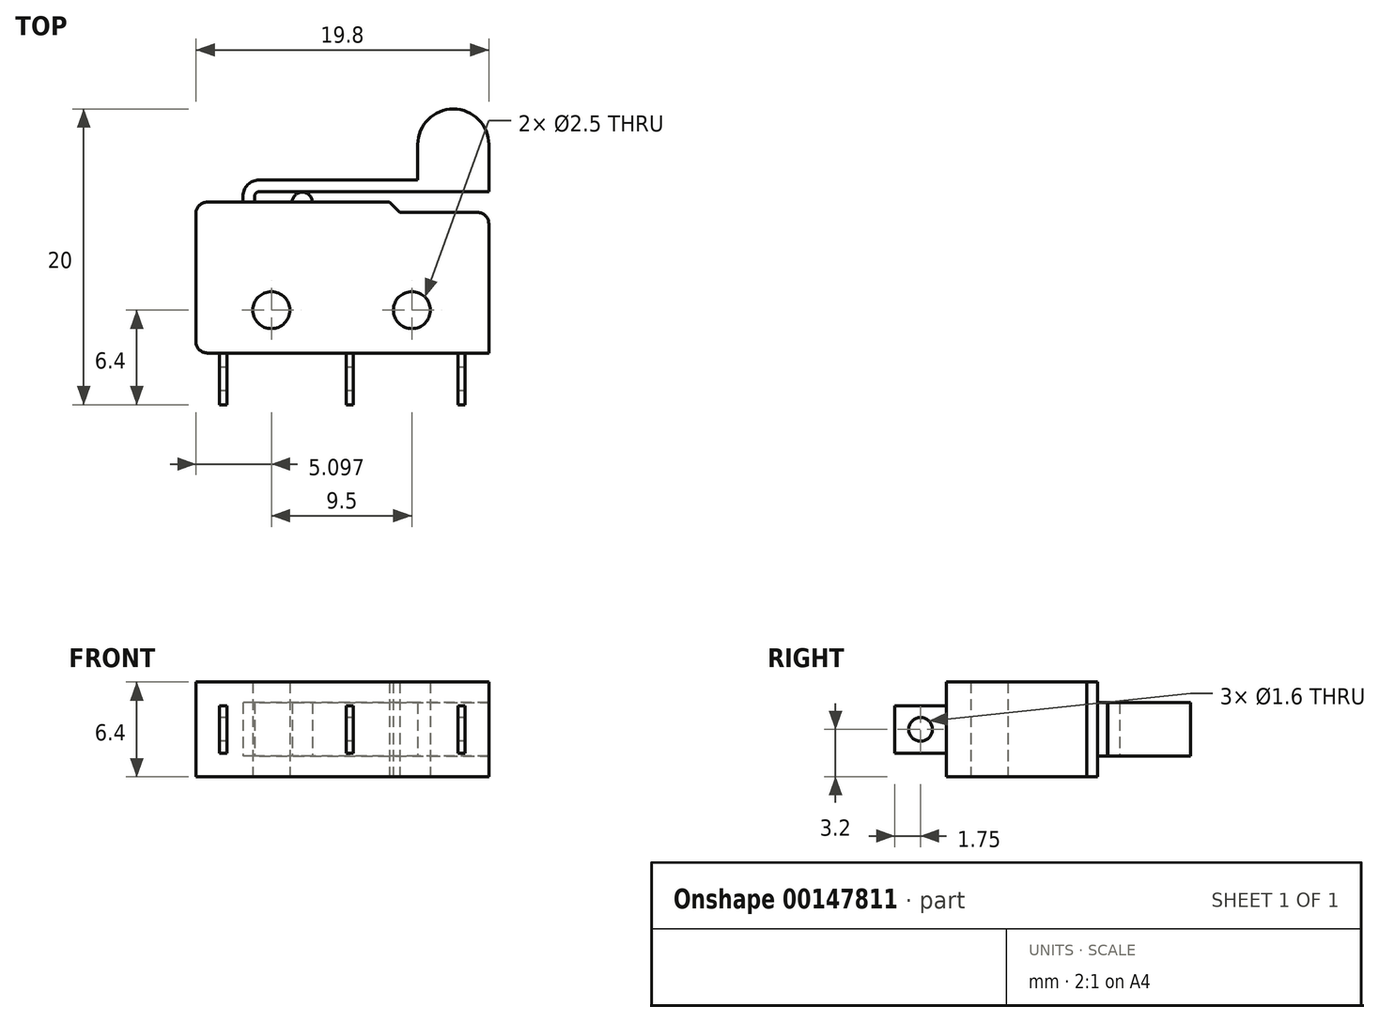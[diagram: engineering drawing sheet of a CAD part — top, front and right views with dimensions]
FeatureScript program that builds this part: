
annotation { "Feature Type Name" : "Feature", "Feature Type Description" : "" }
export const myFeature = defineFeature(function(context is Context, id is Id, definition is map)
    precondition{}
    {
        {
            var Q0;
            Q0=qCreatedBy(makeId("Top.planeOp"),FACE);
            var sketch = newSketch(context, id + "F0", { "sketchPlane" : qUnion([Q0])});
            skLineSegment(sketch, "E0", {"start": v(0, 0) * mm, "end": v(6.02, 0) * mm});
            skLineSegment(sketch, "E1", {"start": v(6.02, 0) * mm, "end": v(6.02, -9.5) * mm});
            skLineSegment(sketch, "E2", {"start": v(0, 0) * mm, "end": v(-0.7, 0.7) * mm});
            skLineSegment(sketch, "E3", {"start": v(6.02, 0) * mm, "end": v(6.02, 0.7) * mm, "construction": true});
            skLineSegment(sketch, "E4", {"start": v(-0.7, 0.7) * mm, "end": v(6.02, 0.7) * mm, "construction": true});
            skLineSegment(sketch, "E5.bottom", {"start": v(4.42, -9.5) * mm, "end": v(3.92, -9.5) * mm});
            skLineSegment(sketch, "E5.top", {"start": v(4.42, -13) * mm, "end": v(3.92, -13) * mm});
            skLineSegment(sketch, "E5.left", {"start": v(3.92, -9.5) * mm, "end": v(3.92, -13) * mm});
            skLineSegment(sketch, "E5.right", {"start": v(4.42, -9.5) * mm, "end": v(4.42, -13) * mm});
            skLineSegment(sketch, "E6.bottom", {"start": v(-3.13, -9.5) * mm, "end": v(-3.63, -9.5) * mm});
            skLineSegment(sketch, "E6.top", {"start": v(-3.13, -13) * mm, "end": v(-3.63, -13) * mm});
            skLineSegment(sketch, "E6.left", {"start": v(-3.13, -9.5) * mm, "end": v(-3.13, -13) * mm});
            skLineSegment(sketch, "E6.right", {"start": v(-3.63, -9.5) * mm, "end": v(-3.63, -13) * mm});
            skLineSegment(sketch, "E7.top", {"start": v(-11.68, -13) * mm, "end": v(-12.18, -13) * mm});
            skLineSegment(sketch, "E7.left", {"start": v(-12.18, -9.5) * mm, "end": v(-12.18, -13) * mm});
            skLineSegment(sketch, "E7.right", {"start": v(-11.68, -9.5) * mm, "end": v(-11.68, -13) * mm});
            skLineSegment(sketch, "E8", {"start": v(-0.7, 0.7) * mm, "end": v(-5.91, 0.7) * mm});
            skLineSegment(sketch, "E9", {"start": v(-5.91, 0.7) * mm, "end": v(-7.27, 0.7) * mm, "construction": true});
            skArc(sketch, "E10", {"start": v(-5.91, 0.7) * mm, "mid": v(-6.6, 1.38) * mm, "end": v(-7.27, 0.7) * mm});
            skLineSegment(sketch, "E11", {"start": v(-7.27, 0.7) * mm, "end": v(-9.81, 0.7) * mm});
            skLineSegment(sketch, "E12", {"start": v(-9.81, 0.7) * mm, "end": v(-9.81, 1.1) * mm});
            skArc(sketch, "E13", {"start": v(-9.51, 1.4) * mm, "mid": v(-9.73, 1.32) * mm, "end": v(-9.81, 1.1) * mm});
            skLineSegment(sketch, "E14", {"start": v(-9.51, 1.4) * mm, "end": v(6.02, 1.4) * mm});
            skLineSegment(sketch, "E15", {"start": v(6.02, 1.4) * mm, "end": v(6.02, 2.2) * mm});
            skLineSegment(sketch, "E16", {"start": v(1.22, 2.2) * mm, "end": v(-9.51, 2.2) * mm});
            skArc(sketch, "E17", {"start": v(-9.51, 2.2) * mm, "mid": v(-10.29, 1.88) * mm, "end": v(-10.6, 1.1) * mm});
            skLineSegment(sketch, "E18", {"start": v(-10.6, 1.1) * mm, "end": v(-10.6, 0.7) * mm});
            skLineSegment(sketch, "E19", {"start": v(-10.6, 0.7) * mm, "end": v(-9.81, 0.7) * mm});
            skLineSegment(sketch, "E20", {"start": v(-8.68, -9.5) * mm, "end": v(-8.68, -6.6) * mm, "construction": true});
            skLineSegment(sketch, "E21", {"start": v(-8.68, -6.6) * mm, "end": v(-13.78, -6.6) * mm, "construction": true});
            skLineSegment(sketch, "E22", {"start": v(-13.78, -9.5) * mm, "end": v(-13.78, 0.7) * mm});
            skCircle(sketch, "E23", {"center": v(-8.68, -6.6) * mm, "radius": 1.25 * mm});
            skLineSegment(sketch, "E24", {"start": v(-8.68, -6.6) * mm, "end": v(0.82, -6.6) * mm, "construction": true});
            skCircle(sketch, "E25", {"center": v(0.82, -6.6) * mm, "radius": 1.25 * mm});
            skLineSegment(sketch, "E26", {"start": v(-13.78, -9.5) * mm, "end": v(-12.18, -9.5) * mm});
            skLineSegment(sketch, "E27", {"start": v(-12.18, -9.5) * mm, "end": v(-11.68, -9.5) * mm});
            skLineSegment(sketch, "E28", {"start": v(-11.68, -9.5) * mm, "end": v(-3.63, -9.5) * mm});
            skPoint(sketch, "E29", {"position": v(-3.38, -13) * mm});
            skLineSegment(sketch, "E30", {"start": v(6.02, -9.5) * mm, "end": v(4.42, -9.5) * mm});
            skLineSegment(sketch, "E31", {"start": v(3.92, -9.5) * mm, "end": v(-3.13, -9.5) * mm});
            skLineSegment(sketch, "E32", {"start": v(-13.78, 0.7) * mm, "end": v(-10.6, 0.7) * mm});
            skLineSegment(sketch, "E33.bottom", {"start": v(6.02, 2.2) * mm, "end": v(1.22, 2.2) * mm, "construction": true});
            skLineSegment(sketch, "E33.top", {"start": v(6.02, 4.6) * mm, "end": v(1.22, 4.6) * mm, "construction": true});
            skLineSegment(sketch, "E33.left", {"start": v(6.02, 2.2) * mm, "end": v(6.02, 4.6) * mm});
            skLineSegment(sketch, "E33.right", {"start": v(1.22, 2.2) * mm, "end": v(1.22, 4.6) * mm});
            skArc(sketch, "E34", {"start": v(6.02, 4.6) * mm, "mid": v(3.62, 7) * mm, "end": v(1.22, 4.6) * mm});
            skArc(sketch, "E35", {"start": v(1.22, 4.6) * mm, "mid": v(3.62, 2.2) * mm, "end": v(6.02, 4.6) * mm, "construction": true});
            skSolve(sketch);
        }
        {
            var Q0;
            Q0=makeQuery(id+"F0.imprint","IMPRINT",FACE,{"disambiguationData":[TD([[makeQuery(id+"F0.imprint","IMPRINT",EDGE,{"derivedFrom":sQuery(id+"F0.wireOp",EDGE,"E5.bottom")}),1.0]])]});
            var Q1;
            Q1=makeQuery(id+"F0.imprint","IMPRINT",FACE,{"disambiguationData":[TD([[makeQuery(id+"F0.imprint","IMPRINT",EDGE,{"derivedFrom":sQuery(id+"F0.wireOp",EDGE,"E6.bottom")}),1.0]])]});
            var Q2;
            Q2=makeQuery(id+"F0.imprint","IMPRINT",FACE,{"disambiguationData":[TD([[makeQuery(id+"F0.imprint","IMPRINT",EDGE,{"derivedFrom":sQuery(id+"F0.wireOp",EDGE,"E7.top")}),-1.0]])]});
            var Q3;
            Q3=makeQuery(id+"F0.imprint","IMPRINT",FACE,{"disambiguationData":[TD([[makeQuery(id+"F0.imprint","IMPRINT",EDGE,{"derivedFrom":sQuery(id+"F0.wireOp",EDGE,"E12")}),1.0]])]});
            var Q4;
            Q4=makeQuery(id+"F0.imprint","IMPRINT",FACE,{"disambiguationData":[TD([[makeQuery(id+"F0.imprint","IMPRINT",EDGE,{"derivedFrom":sQuery(id+"F0.wireOp",EDGE,"E0")}),-1.0]])]});
            var Q5;
            {var subQ1=sQuery(id+"F0.wireOp",EDGE,"E11");Q5=makeQuery(id+"F0.imprint","IMPRINT",FACE,{"disambiguationData":[TD([[makeQuery(id+"F0.imprint","IMPRINT",EDGE,{"derivedFrom":subQ1}),-1.0]])]});}
            extrude(context, id + "F1", {"entities" : qUnion([Q0, Q1, Q2, Q3, Q4, Q5]), "depth" : 6.4 * mm});
        }
        {
            var Q0;
            Q0=makeQuery(id+"F1.opExtrude","SWEPT_FACE",FACE,{"disambiguationData":[OSD([sQuery(id+"F0.wireOp",EDGE,"E22")])]});
            var sketch = newSketch(context, id + "F2", { "sketchPlane" : qUnion([Q0])});
            skLineSegment(sketch, "E36.bottom", {"start": v(-0.7, 0) * mm, "end": v(-26.1, 0) * mm});
            skLineSegment(sketch, "E36.top", {"start": v(-0.7, 1.4) * mm, "end": v(-26.1, 1.4) * mm});
            skLineSegment(sketch, "E36.left", {"start": v(-0.7, 0) * mm, "end": v(-0.7, 1.4) * mm});
            skLineSegment(sketch, "E36.right", {"start": v(-26.1, 0) * mm, "end": v(-26.1, 1.4) * mm});
            skLineSegment(sketch, "E37.bottom", {"start": v(-0.7, 6.4) * mm, "end": v(-26.1, 6.4) * mm});
            skLineSegment(sketch, "E37.top", {"start": v(-0.7, 5) * mm, "end": v(-26.1, 5) * mm});
            skLineSegment(sketch, "E37.left", {"start": v(-0.7, 6.4) * mm, "end": v(-0.7, 5) * mm});
            skLineSegment(sketch, "E37.right", {"start": v(-26.1, 6.4) * mm, "end": v(-26.1, 5) * mm});
            skLineSegment(sketch, "E38", {"start": v(-26.1, 1.4) * mm, "end": v(-26.1, 5) * mm, "construction": true});
            skPoint(sketch, "E39", {"position": v(-2.2, 3.2) * mm});
            skLineSegment(sketch, "E40.bottom", {"start": v(9.5, 0) * mm, "end": v(13, 0) * mm});
            skLineSegment(sketch, "E40.top", {"start": v(9.5, 1.6) * mm, "end": v(13, 1.6) * mm});
            skLineSegment(sketch, "E40.left", {"start": v(9.5, 0) * mm, "end": v(9.5, 1.6) * mm});
            skLineSegment(sketch, "E40.right", {"start": v(13, 0) * mm, "end": v(13, 1.6) * mm});
            skLineSegment(sketch, "E41.bottom", {"start": v(9.5, 6.4) * mm, "end": v(13, 6.4) * mm});
            skLineSegment(sketch, "E41.top", {"start": v(9.5, 4.8) * mm, "end": v(13, 4.8) * mm});
            skLineSegment(sketch, "E41.left", {"start": v(9.5, 6.4) * mm, "end": v(9.5, 4.8) * mm});
            skLineSegment(sketch, "E41.right", {"start": v(13, 6.4) * mm, "end": v(13, 4.8) * mm});
            skLineSegment(sketch, "E42", {"start": v(13, 1.6) * mm, "end": v(13, 4.8) * mm, "construction": true});
            skPoint(sketch, "E43", {"position": v(13, 3.2) * mm});
            skLineSegment(sketch, "E44", {"start": v(13, 3.2) * mm, "end": v(9.5, 3.2) * mm, "construction": true});
            skCircle(sketch, "E45", {"center": v(11.25, 3.2) * mm, "radius": 0.8 * mm});
            skSolve(sketch);
        }
        {
            var Q0;
            Q0=qSketchRegion(id+"F2",true);
            var Q1;
            Q1=makeQuery(id+"F1.opExtrude","SWEPT_FACE",FACE,{"disambiguationData":[OSD([sQuery(id+"F0.wireOp",EDGE,"E15")])]});
            extrude(context, id + "F3", {"entities" : qUnion([Q0]), "operationType" : NewBodyOperationType.REMOVE, "endBound" : BoundingType.UP_TO_SURFACE, "oppositeDirection" : true, "endBoundEntityFace" : qUnion([Q1]), "depth" : 25.4 * mm});
        }
        {
            var Q0;
            Q0=makeQuery(id+"F3.boolean.opBoolean","INTERSECT",EDGE,{"derivedFrom":[makeQuery(id+"F3.opExtrude","SWEPT_FACE",FACE,{"disambiguationData":[OSD([sQuery(id+"F2.wireOp",EDGE,"E40.left")])]}),makeQuery(id+"F3.opExtrude","SWEPT_FACE",FACE,{"disambiguationData":[OSD([sQuery(id+"F2.wireOp",EDGE,"E41.left")])]})]});
            var Q1;
            Q1=makeQuery(id+"F1.opExtrude","SWEPT_EDGE",EDGE,{"disambiguationData":[OSD([sQuery(id+"F0.wireOp",EDGE,"E0"),sQuery(id+"F0.wireOp",EDGE,"E1")])]});
            var Q2;
            Q2=makeQuery(id+"F1.opExtrude","SWEPT_EDGE",EDGE,{"disambiguationData":[OSD([sQuery(id+"F0.wireOp",EDGE,"E22"),sQuery(id+"F0.wireOp",EDGE,"E26")])]});
            var Q3;
            Q3=makeQuery(id+"F1.opExtrude","SWEPT_EDGE",EDGE,{"disambiguationData":[OSD([sQuery(id+"F0.wireOp",EDGE,"E22"),sQuery(id+"F0.wireOp",EDGE,"E32")])]});
            fillet(context, id + "F4", {"entities" : qUnion([Q0, Q1, Q2, Q3]), "radius" : 0.76 * mm, "tangentPropagation" : true, "allowEdgeOverflow" : false});
        }
    });
